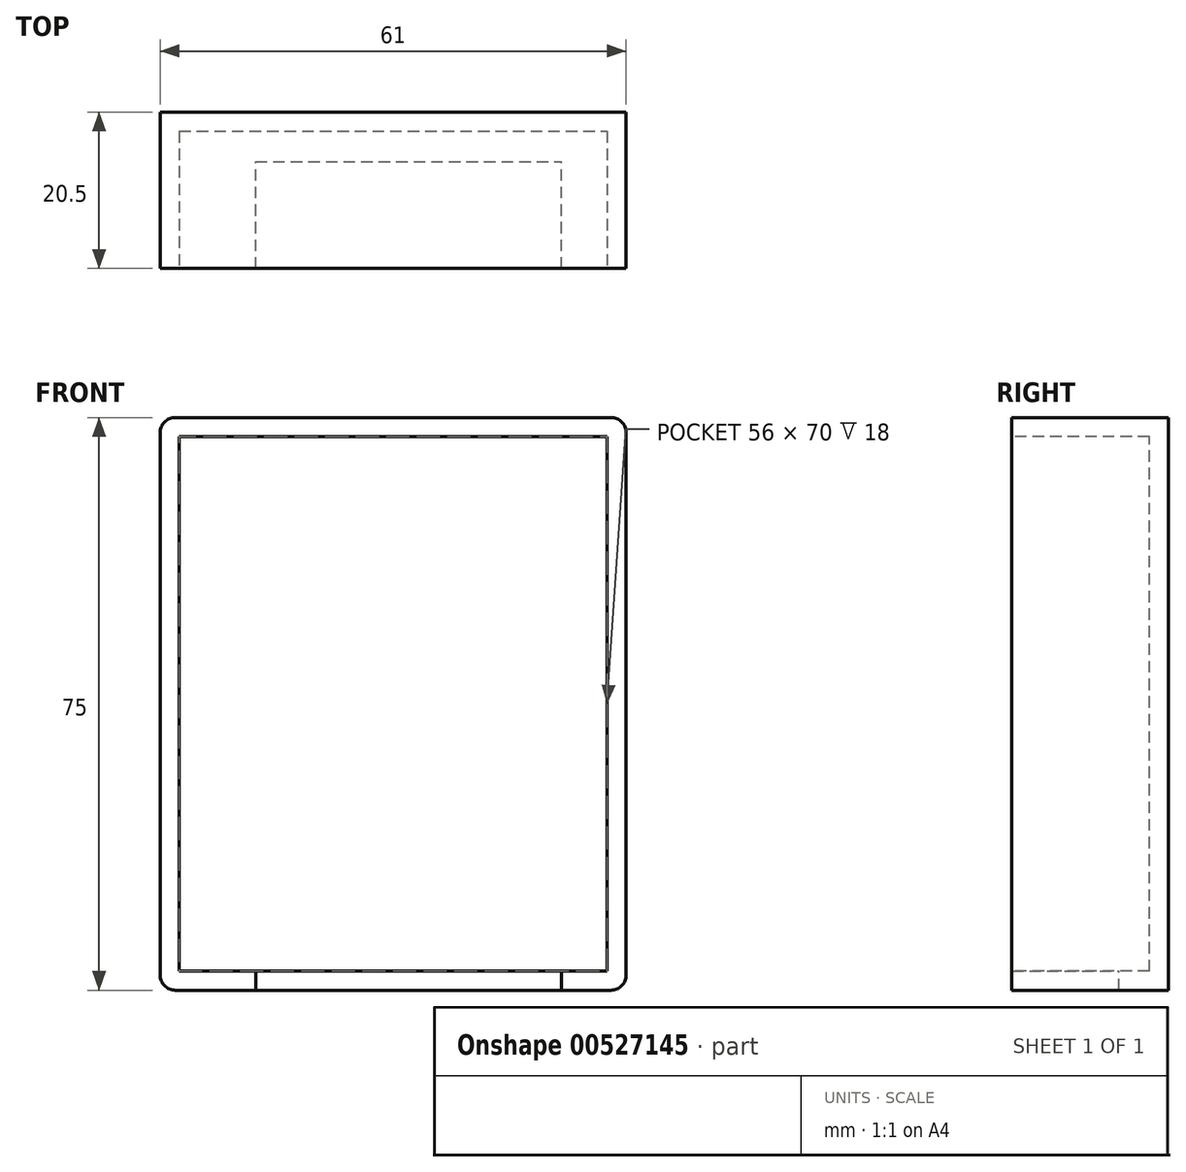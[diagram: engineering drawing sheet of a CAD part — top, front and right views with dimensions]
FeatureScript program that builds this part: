
annotation { "Feature Type Name" : "Feature", "Feature Type Description" : "" }
export const myFeature = defineFeature(function(context is Context, id is Id, definition is map)
    precondition{}
    {
        {
            var Q0;
            Q0=qCreatedBy(makeId("Front.planeOp"),FACE);
            var sketch = newSketch(context, id + "F0", { "sketchPlane" : qUnion([Q0])});
            skLineSegment(sketch, "E0.bottom", {"start": v(0, 0) * mm, "end": v(61, 0) * mm});
            skLineSegment(sketch, "E0.top", {"start": v(0, 75) * mm, "end": v(61, 75) * mm});
            skLineSegment(sketch, "E0.left", {"start": v(0, 0) * mm, "end": v(0, 75) * mm});
            skLineSegment(sketch, "E0.right", {"start": v(61, 0) * mm, "end": v(61, 75) * mm});
            skSolve(sketch);
        }
        {
            var Q0;
            Q0 = qSketchRegion(id + "F0", true);
            extrude(context, id + "F1", {"entities" : qUnion([Q0]), "depth" : 20.5 * mm, "offsetDistance" : 25 * mm});
        }
        {
            var Q0;
            Q0=makeQuery(id+"F1.opExtrude","SWEPT_EDGE",EDGE,{"disambiguationData":[OSD([sQuery(id+"F0.wireOp",EDGE,"E0.top"),sQuery(id+"F0.wireOp",EDGE,"E0.left")])]});
            var Q1;
            Q1=makeQuery(id+"F1.opExtrude","SWEPT_EDGE",EDGE,{"disambiguationData":[OSD([sQuery(id+"F0.wireOp",EDGE,"E0.top"),sQuery(id+"F0.wireOp",EDGE,"E0.right")])]});
            var Q2;
            Q2=makeQuery(id+"F1.opExtrude","SWEPT_EDGE",EDGE,{"disambiguationData":[OSD([sQuery(id+"F0.wireOp",EDGE,"E0.bottom"),sQuery(id+"F0.wireOp",EDGE,"E0.right")])]});
            var Q3;
            Q3=makeQuery(id+"F1.opExtrude","SWEPT_EDGE",EDGE,{"disambiguationData":[OSD([sQuery(id+"F0.wireOp",EDGE,"E0.bottom"),sQuery(id+"F0.wireOp",EDGE,"E0.left")])]});
            fillet(context, id + "F2", {"entities" : qUnion([Q0, Q1, Q2, Q3]), "radius" : 2 * mm, "tangentPropagation" : true, "allowEdgeOverflow" : false});
        }
        {
            var Q0;
            Q0=makeQuery(id+"F1.opExtrude","CAP_FACE",FACE,{"disambiguationData":[OSD([sQuery(id+"F0.wireOp",EDGE,"E0.bottom"),sQuery(id+"F0.wireOp",EDGE,"E0.top"),sQuery(id+"F0.wireOp",EDGE,"E0.left"),sQuery(id+"F0.wireOp",EDGE,"E0.right")])],"isStart":false});
            shell(context, id + "F3", {"entities" : qUnion([Q0]), "thickness" : 2.5 * mm});
        }
        {
            var Q0;
            Q0=makeQuery(id+"F3.opShell","OFFSET_FACE",FACE,{"disambiguationData":[OSD([sQuery(id+"F0.wireOp",EDGE,"E0.bottom")])]});
            var sketch = newSketch(context, id + "F4", { "sketchPlane" : qUnion([Q0])});
            skLineSegment(sketch, "E1.bottom", {"start": v(12.5, -20.5) * mm, "end": v(52.5, -20.5) * mm});
            skLineSegment(sketch, "E1.top", {"start": v(12.5, -6.5) * mm, "end": v(52.5, -6.5) * mm});
            skLineSegment(sketch, "E1.left", {"start": v(12.5, -20.5) * mm, "end": v(12.5, -6.5) * mm});
            skLineSegment(sketch, "E1.right", {"start": v(52.5, -20.5) * mm, "end": v(52.5, -6.5) * mm});
            skSolve(sketch);
        }
        {
            var Q0;
            Q0 = qSketchRegion(id + "F4", true);
            extrude(context, id + "F5", {"entities" : qUnion([Q0]), "operationType" : NewBodyOperationType.REMOVE, "oppositeDirection" : true, "depth" : 25 * mm, "offsetDistance" : 25 * mm});
        }
    });
